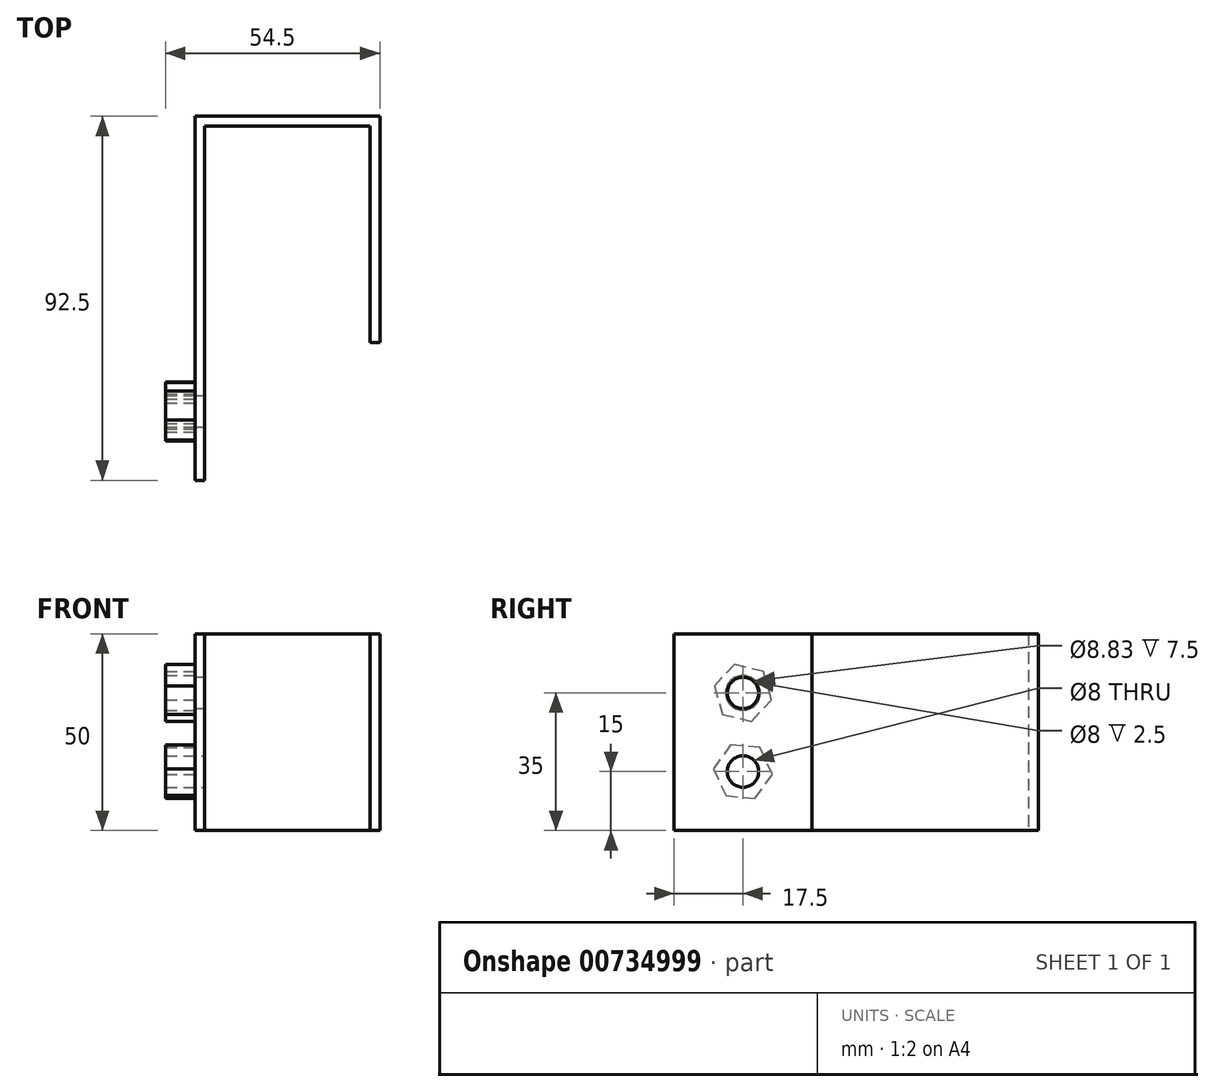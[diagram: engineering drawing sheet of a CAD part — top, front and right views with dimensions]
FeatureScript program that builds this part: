
annotation { "Feature Type Name" : "Feature", "Feature Type Description" : "" }
export const myFeature = defineFeature(function(context is Context, id is Id, definition is map)
    precondition{}
    {
        {
            var Q0;
            Q0=qCreatedBy(makeId("Top.planeOp"),FACE);
            var sketch = newSketch(context, id + "F0", { "sketchPlane" : qUnion([Q0])});
            skLineSegment(sketch, "E0", {"start": v(0, 0) * mm, "end": v(0, 92.5) * mm});
            skLineSegment(sketch, "E1", {"start": v(0, 92.5) * mm, "end": v(47, 92.5) * mm});
            skLineSegment(sketch, "E2", {"start": v(47, 92.5) * mm, "end": v(47, 35) * mm});
            skLineSegment(sketch, "E3", {"start": v(47, 35) * mm, "end": v(44.5, 35) * mm});
            skLineSegment(sketch, "E4", {"start": v(44.5, 35) * mm, "end": v(44.5, 90) * mm});
            skLineSegment(sketch, "E5", {"start": v(44.5, 90) * mm, "end": v(2.5, 90) * mm});
            skLineSegment(sketch, "E6", {"start": v(2.5, 90) * mm, "end": v(2.5, 0) * mm});
            skLineSegment(sketch, "E7", {"start": v(2.5, 0) * mm, "end": v(0, 0) * mm});
            skSolve(sketch);
        }
        {
            var Q0;
            Q0 = qSketchRegion(id + "F0", true);
            extrude(context, id + "F1", {"entities" : qUnion([Q0]), "depth" : 50 * mm, "offsetDistance" : 25 * mm});
        }
        {
            var Q0;
            Q0=makeQuery(id+"F1.opExtrude","SWEPT_FACE",FACE,{"disambiguationData":[OSD([sQuery(id+"F0.wireOp",EDGE,"E6")])]});
            var sketch = newSketch(context, id + "F2", { "sketchPlane" : qUnion([Q0])});
            skLineSegment(sketch, "E8", {"start": v(17.5, 50) * mm, "end": v(17.5, 35) * mm});
            skLineSegment(sketch, "E9", {"start": v(17.5, 35) * mm, "end": v(17.5, 15) * mm});
            skCircle(sketch, "E10.cCircle", {"center": v(17.5, 35) * mm, "radius": 6.5 * mm, "construction": true});
            skLineSegment(sketch, "E10.0", {"start": v(24.8, 33.23) * mm, "end": v(19.61, 27.8) * mm});
            skLineSegment(sketch, "E10.1", {"start": v(19.61, 27.8) * mm, "end": v(12.32, 29.57) * mm});
            skLineSegment(sketch, "E10.2", {"start": v(12.32, 29.57) * mm, "end": v(10.2, 36.77) * mm});
            skLineSegment(sketch, "E10.3", {"start": v(10.2, 36.77) * mm, "end": v(15.39, 42.2) * mm});
            skLineSegment(sketch, "E10.4", {"start": v(15.39, 42.2) * mm, "end": v(22.68, 40.43) * mm});
            skLineSegment(sketch, "E10.5", {"start": v(22.68, 40.43) * mm, "end": v(24.8, 33.23) * mm});
            skPoint(sketch, "E10.0.midPoint", {"position": v(22.2, 30.51) * mm});
            skCircle(sketch, "E11.cCircle", {"center": v(17.5, 15) * mm, "radius": 6.5 * mm, "construction": true});
            skLineSegment(sketch, "E11.0", {"start": v(24.97, 14.28) * mm, "end": v(20.61, 8.17) * mm});
            skLineSegment(sketch, "E11.1", {"start": v(20.61, 8.17) * mm, "end": v(13.14, 8.89) * mm});
            skLineSegment(sketch, "E11.2", {"start": v(13.14, 8.89) * mm, "end": v(10.03, 15.72) * mm});
            skLineSegment(sketch, "E11.3", {"start": v(10.03, 15.72) * mm, "end": v(14.39, 21.83) * mm});
            skLineSegment(sketch, "E11.4", {"start": v(14.39, 21.83) * mm, "end": v(21.86, 21.11) * mm});
            skLineSegment(sketch, "E11.5", {"start": v(21.86, 21.11) * mm, "end": v(24.97, 14.28) * mm});
            skPoint(sketch, "E11.0.midPoint", {"position": v(22.8, 11.23) * mm});
            skCircle(sketch, "E12", {"center": v(17.5, 35) * mm, "radius": 4.42 * mm});
            skCircle(sketch, "E13", {"center": v(17.5, 15) * mm, "radius": 3.8 * mm});
            skSolve(sketch);
        }
        {
            var Q0;
            Q0 = qSketchRegion(id + "F2", true);
            extrude(context, id + "F3", {"entities" : qUnion([Q0]), "operationType" : NewBodyOperationType.ADD, "oppositeDirection" : true, "depth" : 10 * mm, "offsetDistance" : 25 * mm});
        }
        {
            var Q0;
            Q0=makeQuery(id+"F1.opExtrude","SWEPT_FACE",FACE,{"disambiguationData":[OSD([sQuery(id+"F0.wireOp",EDGE,"E6")])]});
            var sketch = newSketch(context, id + "F4", { "sketchPlane" : qUnion([Q0])});
            skCircle(sketch, "E14", {"center": v(17.5, 35) * mm, "radius": 4 * mm});
            skCircle(sketch, "E15", {"center": v(17.5, 15) * mm, "radius": 4 * mm});
            skSolve(sketch);
        }
        {
            var Q0;
            Q0 = qSketchRegion(id + "F4", true);
            extrude(context, id + "F5", {"entities" : qUnion([Q0]), "operationType" : NewBodyOperationType.REMOVE, "oppositeDirection" : true, "depth" : 15 * mm, "offsetDistance" : 25 * mm});
        }
    });
